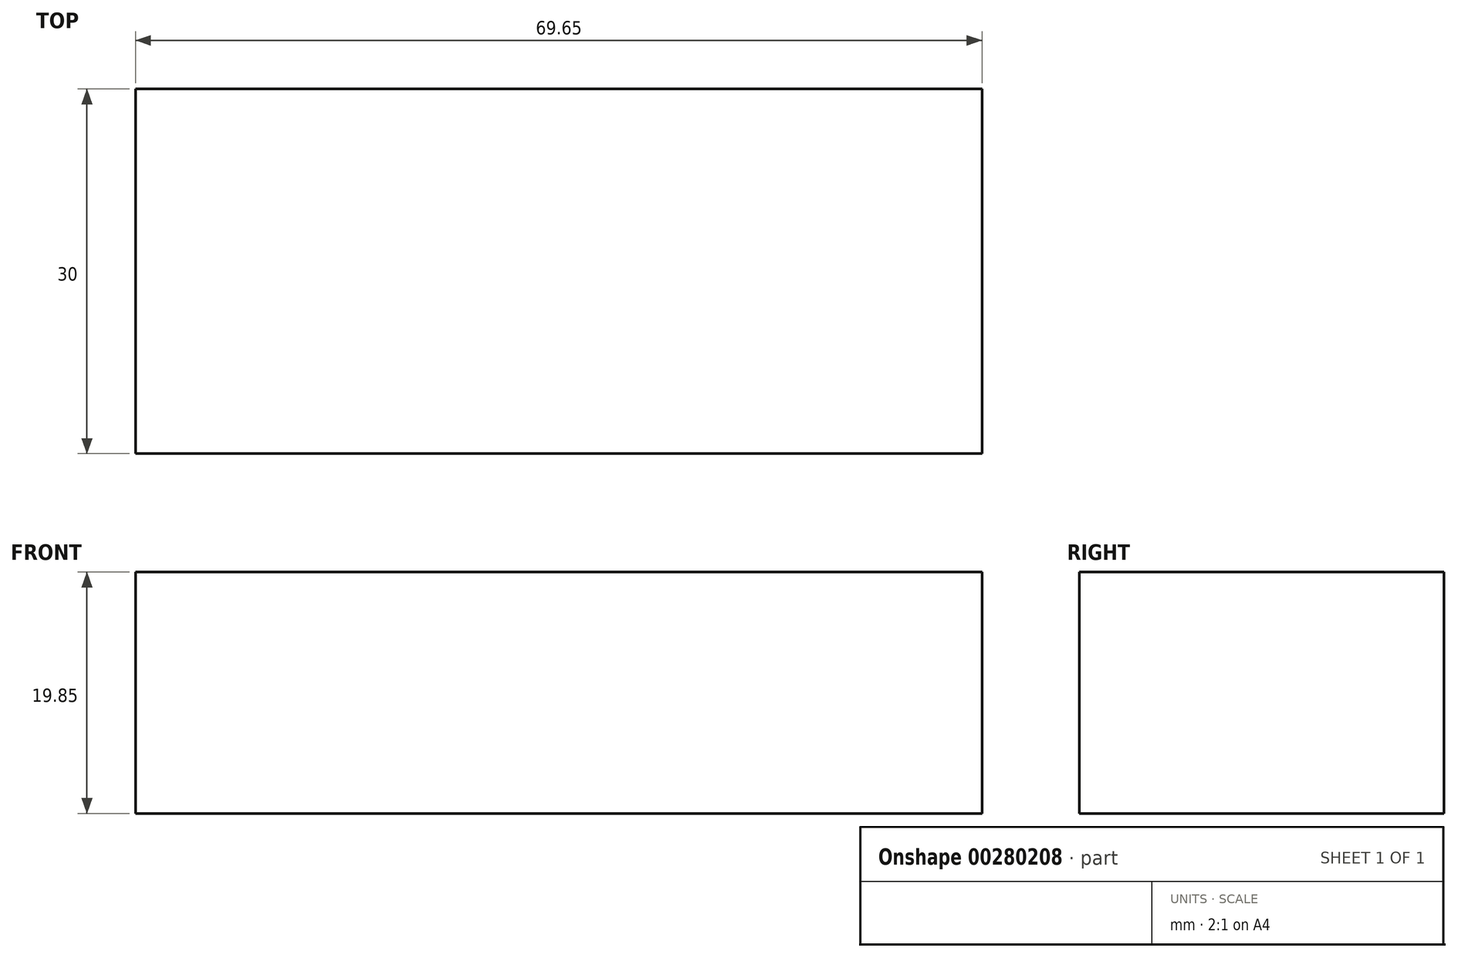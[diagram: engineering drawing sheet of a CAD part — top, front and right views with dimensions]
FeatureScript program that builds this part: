
annotation { "Feature Type Name" : "Feature", "Feature Type Description" : "" }
export const myFeature = defineFeature(function(context is Context, id is Id, definition is map)
    precondition{}
    {
        {
            var Q0;
            Q0=qCreatedBy(makeId("Front.planeOp"),FACE);
            var sketch = newSketch(context, id + "F0", { "sketchPlane" : qUnion([Q0])});
            skLineSegment(sketch, "E0.bottom", {"start": v(0, 0) * mm, "end": v(69.65, 0) * mm});
            skLineSegment(sketch, "E0.top", {"start": v(0, 19.85) * mm, "end": v(69.65, 19.85) * mm});
            skLineSegment(sketch, "E0.left", {"start": v(0, 0) * mm, "end": v(0, 19.85) * mm});
            skLineSegment(sketch, "E0.right", {"start": v(69.65, 0) * mm, "end": v(69.65, 19.85) * mm});
            skSolve(sketch);
        }
        {
            var Q0;
            Q0=qSketchRegion(id+"F0",true);
            extrude(context, id + "F1", {"entities" : qUnion([Q0]), "depth" : 30 * mm});
        }
    });
